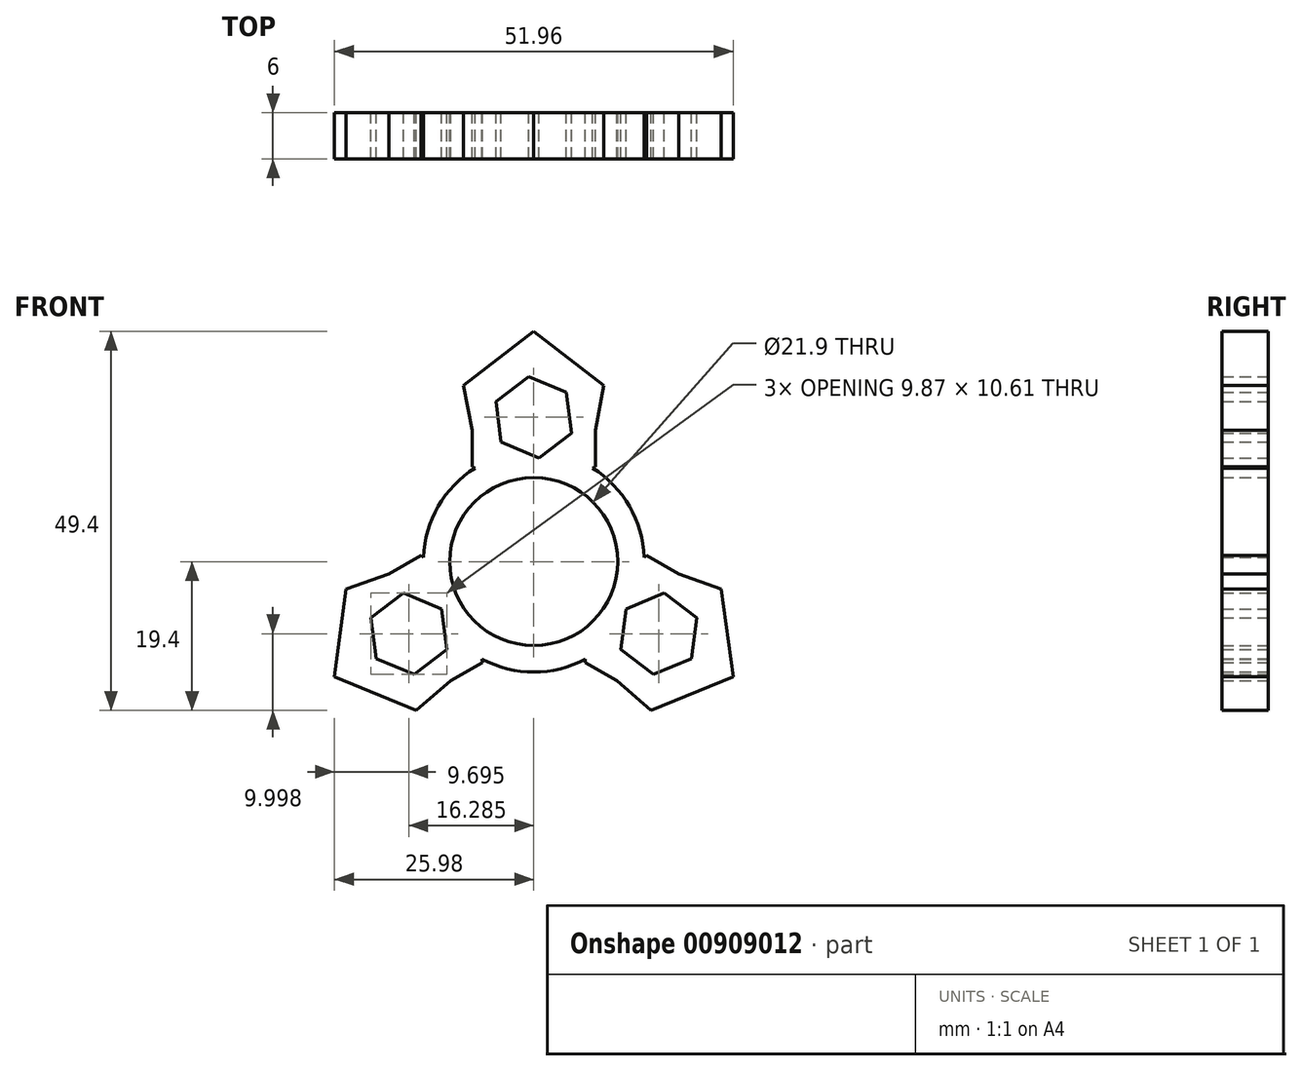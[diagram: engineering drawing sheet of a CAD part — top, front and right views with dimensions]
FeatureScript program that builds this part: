
annotation { "Feature Type Name" : "Feature", "Feature Type Description" : "" }
export const myFeature = defineFeature(function(context is Context, id is Id, definition is map)
    precondition{}
    {
        {
            var Q0;
            Q0=qCreatedBy(makeId("Front.planeOp"),FACE);
            var sketch = newSketch(context, id + "F0", { "sketchPlane" : qUnion([Q0])});
            skCircle(sketch, "E0", {"center": v(0, 0) * mm, "radius": 10.95 * mm});
            skLineSegment(sketch, "E1", {"start": v(0, 0) * mm, "end": v(0, 30) * mm});
            skLineSegment(sketch, "E2", {"start": v(0, 0) * mm, "end": v(25.98, -15) * mm});
            skLineSegment(sketch, "E3", {"start": v(0, 0) * mm, "end": v(-25.98, -15) * mm});
            skCircle(sketch, "E4", {"center": v(0, 0) * mm, "radius": 30 * mm});
            skCircle(sketch, "E5.cCircle", {"center": v(0, 18.8) * mm, "radius": 5.35 * mm, "construction": true});
            skLineSegment(sketch, "E5.0", {"start": v(4.93, 16.74) * mm, "end": v(0.68, 13.5) * mm});
            skLineSegment(sketch, "E5.1", {"start": v(0.68, 13.5) * mm, "end": v(-4.26, 15.56) * mm});
            skLineSegment(sketch, "E5.2", {"start": v(-4.26, 15.56) * mm, "end": v(-4.93, 20.87) * mm});
            skLineSegment(sketch, "E5.3", {"start": v(-4.93, 20.87) * mm, "end": v(-0.68, 24.11) * mm});
            skLineSegment(sketch, "E5.4", {"start": v(-0.68, 24.11) * mm, "end": v(4.26, 22.04) * mm});
            skLineSegment(sketch, "E5.5", {"start": v(4.26, 22.04) * mm, "end": v(4.93, 16.74) * mm});
            skLineSegment(sketch, "E6", {"start": v(0, 30) * mm, "end": v(-9.15, 22.95) * mm});
            skLineSegment(sketch, "E7", {"start": v(-9.15, 22.95) * mm, "end": v(-8.04, 17.15) * mm});
            skLineSegment(sketch, "E8", {"start": v(-8.04, 17.15) * mm, "end": v(-8.04, 12.36) * mm});
            skLineSegment(sketch, "E9", {"start": v(-8.04, 12.36) * mm, "end": v(-3.54, 10.36) * mm});
            skLineSegment(sketch, "E10.MirrorCS", {"start": v(0, 30) * mm, "end": v(9.15, 22.95) * mm});
            skLineSegment(sketch, "E11.MirrorCS", {"start": v(9.15, 22.95) * mm, "end": v(8.04, 17.15) * mm});
            skLineSegment(sketch, "E12.MirrorCS", {"start": v(8.04, 17.15) * mm, "end": v(8.04, 12.36) * mm});
            skLineSegment(sketch, "E13.MirrorCS", {"start": v(8.04, 12.36) * mm, "end": v(3.54, 10.36) * mm});
            skLineSegment(sketch, "E14.MirrorCS", {"start": v(10.83, -15.54) * mm, "end": v(6.68, -13.14) * mm});
            skLineSegment(sketch, "E15.MirrorCS", {"start": v(15.6, -14.7) * mm, "end": v(20.54, -12.64) * mm});
            skLineSegment(sketch, "E16.MirrorCS", {"start": v(20.54, -12.64) * mm, "end": v(21.22, -7.33) * mm});
            skLineSegment(sketch, "E17.MirrorCS", {"start": v(24.45, -3.55) * mm, "end": v(18.87, -1.6) * mm});
            skLineSegment(sketch, "E18.MirrorCS", {"start": v(25.98, -15) * mm, "end": v(15.3, -19.4) * mm});
            skLineSegment(sketch, "E19.MirrorCS", {"start": v(16.96, -4.1) * mm, "end": v(12.03, -6.16) * mm});
            skLineSegment(sketch, "E20.MirrorCS", {"start": v(15.3, -19.4) * mm, "end": v(10.83, -15.54) * mm});
            skLineSegment(sketch, "E21.MirrorCS", {"start": v(14.72, 0.79) * mm, "end": v(10.74, -2.12) * mm});
            skLineSegment(sketch, "E22.MirrorCS", {"start": v(21.22, -7.33) * mm, "end": v(16.96, -4.1) * mm});
            skCircle(sketch, "E23.MirrorC", {"center": v(16.28, -9.4) * mm, "radius": 5.35 * mm, "construction": true});
            skLineSegment(sketch, "E24.MirrorCS", {"start": v(11.35, -11.47) * mm, "end": v(15.6, -14.7) * mm});
            skLineSegment(sketch, "E25.MirrorCS", {"start": v(6.68, -13.14) * mm, "end": v(7.2, -8.24) * mm});
            skLineSegment(sketch, "E26.MirrorCS", {"start": v(25.98, -15) * mm, "end": v(24.45, -3.55) * mm});
            skLineSegment(sketch, "E27.MirrorCS", {"start": v(12.03, -6.16) * mm, "end": v(11.35, -11.47) * mm});
            skLineSegment(sketch, "E28.MirrorCS", {"start": v(18.87, -1.6) * mm, "end": v(14.72, 0.79) * mm});
            skLineSegment(sketch, "E29.MirrorCS", {"start": v(-18.87, -1.6) * mm, "end": v(-14.72, 0.79) * mm});
            skLineSegment(sketch, "E30.MirrorCS", {"start": v(-24.45, -3.55) * mm, "end": v(-18.87, -1.6) * mm});
            skLineSegment(sketch, "E31.MirrorCS", {"start": v(-25.98, -15) * mm, "end": v(-24.45, -3.55) * mm});
            skLineSegment(sketch, "E32.MirrorCS", {"start": v(-25.98, -15) * mm, "end": v(-15.3, -19.4) * mm});
            skLineSegment(sketch, "E33.MirrorCS", {"start": v(-15.3, -19.4) * mm, "end": v(-10.83, -15.54) * mm});
            skLineSegment(sketch, "E34.MirrorCS", {"start": v(-10.83, -15.54) * mm, "end": v(-6.68, -13.14) * mm});
            skLineSegment(sketch, "E35.MirrorCS", {"start": v(-6.68, -13.14) * mm, "end": v(-7.2, -8.24) * mm});
            skLineSegment(sketch, "E36.MirrorCS", {"start": v(-11.35, -11.47) * mm, "end": v(-15.6, -14.7) * mm});
            skLineSegment(sketch, "E37.MirrorCS", {"start": v(-20.54, -12.64) * mm, "end": v(-21.22, -7.33) * mm});
            skLineSegment(sketch, "E38.MirrorCS", {"start": v(-15.6, -14.7) * mm, "end": v(-20.54, -12.64) * mm});
            skLineSegment(sketch, "E39.MirrorCS", {"start": v(-21.22, -7.33) * mm, "end": v(-16.96, -4.1) * mm});
            skCircle(sketch, "E40.MirrorC", {"center": v(-16.28, -9.4) * mm, "radius": 5.35 * mm, "construction": true});
            skLineSegment(sketch, "E41.MirrorCS", {"start": v(-12.03, -6.16) * mm, "end": v(-11.35, -11.47) * mm});
            skLineSegment(sketch, "E42.MirrorCS", {"start": v(-16.96, -4.1) * mm, "end": v(-12.03, -6.16) * mm});
            skLineSegment(sketch, "E43.MirrorCS", {"start": v(-14.72, 0.79) * mm, "end": v(-10.74, -2.12) * mm});
            skArc(sketch, "E44", {"start": v(-7.66, 12.19) * mm, "mid": v(-12.47, 7.2) * mm, "end": v(-14.39, 0.54) * mm});
            skArc(sketch, "E45.trimOffspring", {"start": v(14.39, 0.54) * mm, "mid": v(12.47, 7.2) * mm, "end": v(7.66, 12.19) * mm});
            skArc(sketch, "E46.trimOffspring", {"start": v(-6.72, -12.73) * mm, "mid": v(0, -14.4) * mm, "end": v(6.72, -12.73) * mm});
            skSolve(sketch);
        }
        {
            var Q0;
            {var subQ3=sQuery(id+"F0.wireOp",EDGE,"E44");Q0=makeQuery(id+"F0.imprint","IMPRINT",FACE,{"disambiguationData":[TD([[makeQuery(id+"F0.imprint","IMPRINT",EDGE,{"derivedFrom":subQ3}),1.0]])]});}
            var Q1;
            {var subQ13=sQuery(id+"F0.wireOp",EDGE,"E42.MirrorCS");Q1=makeQuery(id+"F0.imprint","IMPRINT",FACE,{"disambiguationData":[TD([[makeQuery(id+"F0.imprint","IMPRINT",EDGE,{"derivedFrom":subQ13}),1.0]])]});}
            var Q2;
            Q2=makeQuery(id+"F0.imprint","IMPRINT",FACE,{"disambiguationData":[TD([[makeQuery(id+"F0.imprint","IMPRINT",EDGE,{"derivedFrom":sQuery(id+"F0.wireOp",EDGE,"E33.MirrorCS")}),1.0]])]});
            var Q3;
            {var subQ3=sQuery(id+"F0.wireOp",EDGE,"E46.trimOffspring");Q3=makeQuery(id+"F0.imprint","IMPRINT",FACE,{"disambiguationData":[TD([[makeQuery(id+"F0.imprint","IMPRINT",EDGE,{"derivedFrom":subQ3}),1.0]])]});}
            var Q4;
            Q4=makeQuery(id+"F0.imprint","IMPRINT",FACE,{"disambiguationData":[TD([[makeQuery(id+"F0.imprint","IMPRINT",EDGE,{"derivedFrom":sQuery(id+"F0.wireOp",EDGE,"E20.MirrorCS")}),-1.0]])]});
            var Q5;
            {var subQ12=sQuery(id+"F0.wireOp",EDGE,"E22.MirrorCS");Q5=makeQuery(id+"F0.imprint","IMPRINT",FACE,{"disambiguationData":[TD([[makeQuery(id+"F0.imprint","IMPRINT",EDGE,{"derivedFrom":subQ12}),-1.0]])]});}
            var Q6;
            {var subQ3=sQuery(id+"F0.wireOp",EDGE,"E45.trimOffspring");Q6=makeQuery(id+"F0.imprint","IMPRINT",FACE,{"disambiguationData":[TD([[makeQuery(id+"F0.imprint","IMPRINT",EDGE,{"derivedFrom":subQ3}),1.0]])]});}
            var Q7;
            {var subQ4=sQuery(id+"F0.wireOp",EDGE,"E5.0");Q7=makeQuery(id+"F0.imprint","IMPRINT",FACE,{"disambiguationData":[TD([[makeQuery(id+"F0.imprint","IMPRINT",EDGE,{"derivedFrom":subQ4}),1.0]])]});}
            var Q8;
            {var subQ10=sQuery(id+"F0.wireOp",EDGE,"E5.2");Q8=makeQuery(id+"F0.imprint","IMPRINT",FACE,{"disambiguationData":[TD([[makeQuery(id+"F0.imprint","IMPRINT",EDGE,{"derivedFrom":subQ10}),1.0]])]});}
            extrude(context, id + "F1", {"entities" : qUnion([Q0, Q1, Q2, Q3, Q4, Q5, Q6, Q7, Q8]), "depth" : 6 * mm, "offsetDistance" : 25 * mm});
        }
    });
